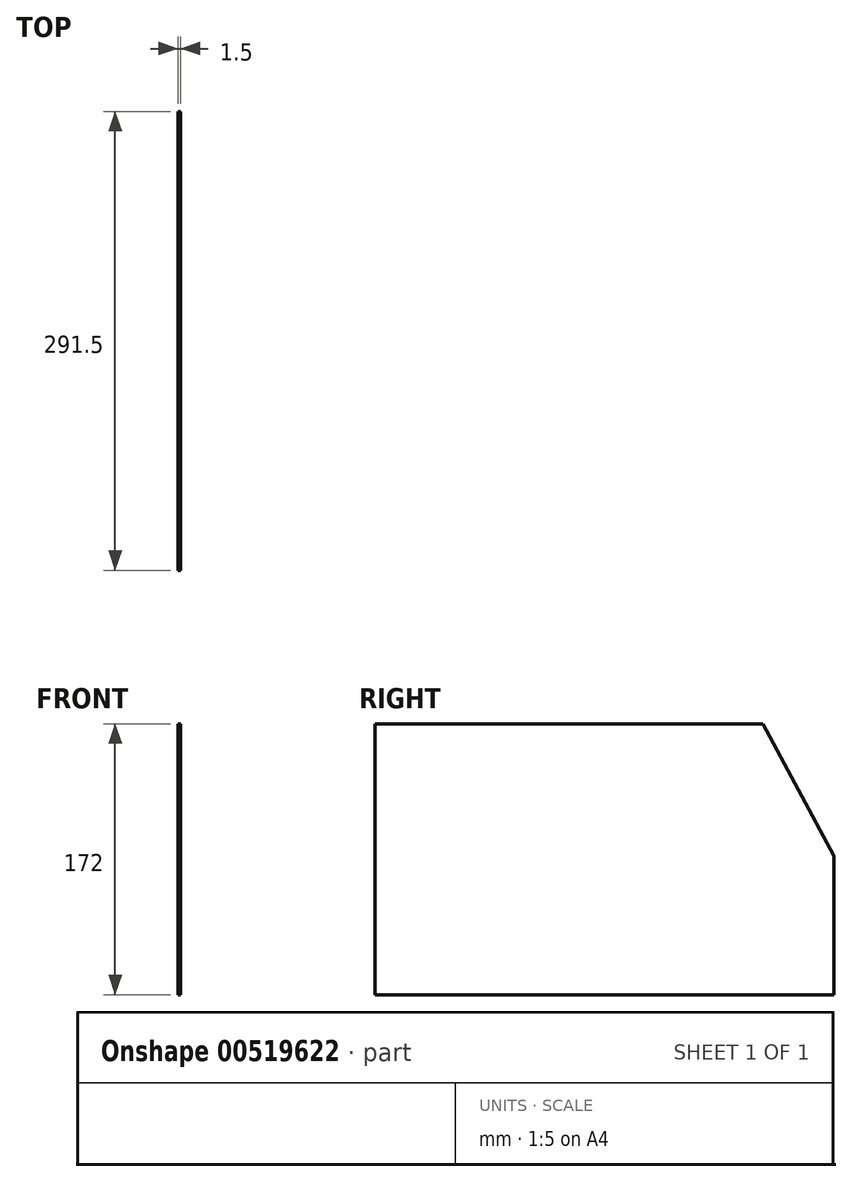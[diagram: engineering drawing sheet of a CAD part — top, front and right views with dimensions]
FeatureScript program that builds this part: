
annotation { "Feature Type Name" : "Feature", "Feature Type Description" : "" }
export const myFeature = defineFeature(function(context is Context, id is Id, definition is map)
    precondition{}
    {
        {
            var Q0;
            Q0=qCreatedBy(makeId("Right.planeOp"),FACE);
            var sketch = newSketch(context, id + "F0", { "sketchPlane" : qUnion([Q0])});
            skLineSegment(sketch, "E0.bottom", {"start": v(101.5, 86) * mm, "end": v(-145, 86) * mm});
            skLineSegment(sketch, "E0.top", {"start": v(146.5, -86) * mm, "end": v(-145, -86) * mm});
            skLineSegment(sketch, "E0.left", {"start": v(146.5, 2) * mm, "end": v(146.5, -42) * mm});
            skLineSegment(sketch, "E0.right", {"start": v(-145, 86) * mm, "end": v(-145, -86) * mm});
            skPoint(sketch, "E0.middle", {"position": v(0.75, 0) * mm});
            skLineSegment(sketch, "E1", {"start": v(101.5, 86) * mm, "end": v(146.5, 2) * mm});
            skLineSegment(sketch, "E2.trimOffspring", {"start": v(146.5, -60) * mm, "end": v(146.5, -86) * mm});
            skLineSegment(sketch, "E3", {"start": v(146.5, -42) * mm, "end": v(146.5, -60) * mm});
            skSolve(sketch);
        }
        {
            var Q0;
            Q0=qSketchRegion(id+"F0",true);
            extrude(context, id + "F1", {"entities" : qUnion([Q0]), "depth" : 1.5 * mm, "offsetDistance" : 25 * mm});
        }
    });
